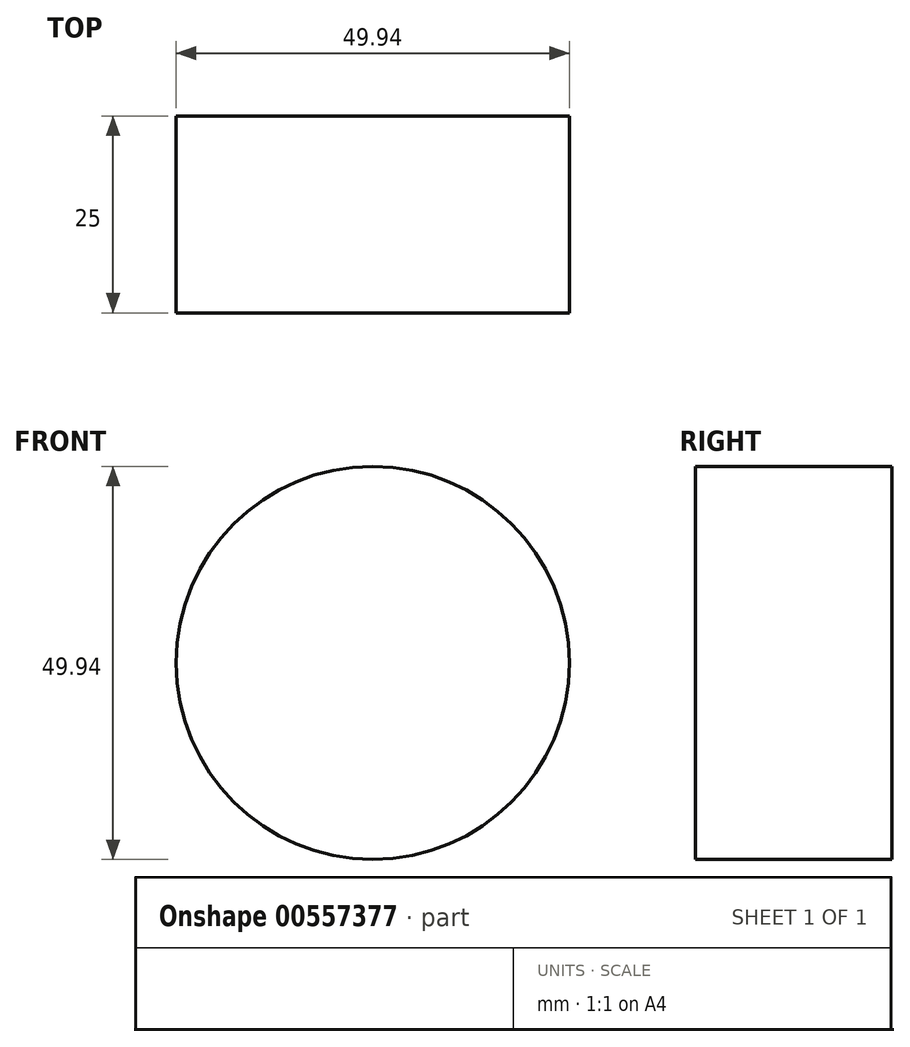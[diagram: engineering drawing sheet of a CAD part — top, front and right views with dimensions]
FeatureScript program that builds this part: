
annotation { "Feature Type Name" : "Feature", "Feature Type Description" : "" }
export const myFeature = defineFeature(function(context is Context, id is Id, definition is map)
    precondition{}
    {
        {
            var Q0;
            Q0=qCreatedBy(makeId("Front.planeOp"),FACE);
            var sketch = newSketch(context, id + "F0", { "sketchPlane" : qUnion([Q0])});
            skCircle(sketch, "E0", {"center": v(0, 0) * mm, "radius": 24.97 * mm});
            skSolve(sketch);
        }
        {
            var Q0;
            Q0 = qSketchRegion(id + "F0", true);
            extrude(context, id + "F1", {"entities" : qUnion([Q0]), "depth" : 25 * mm, "offsetDistance" : 25 * mm});
        }
    });
